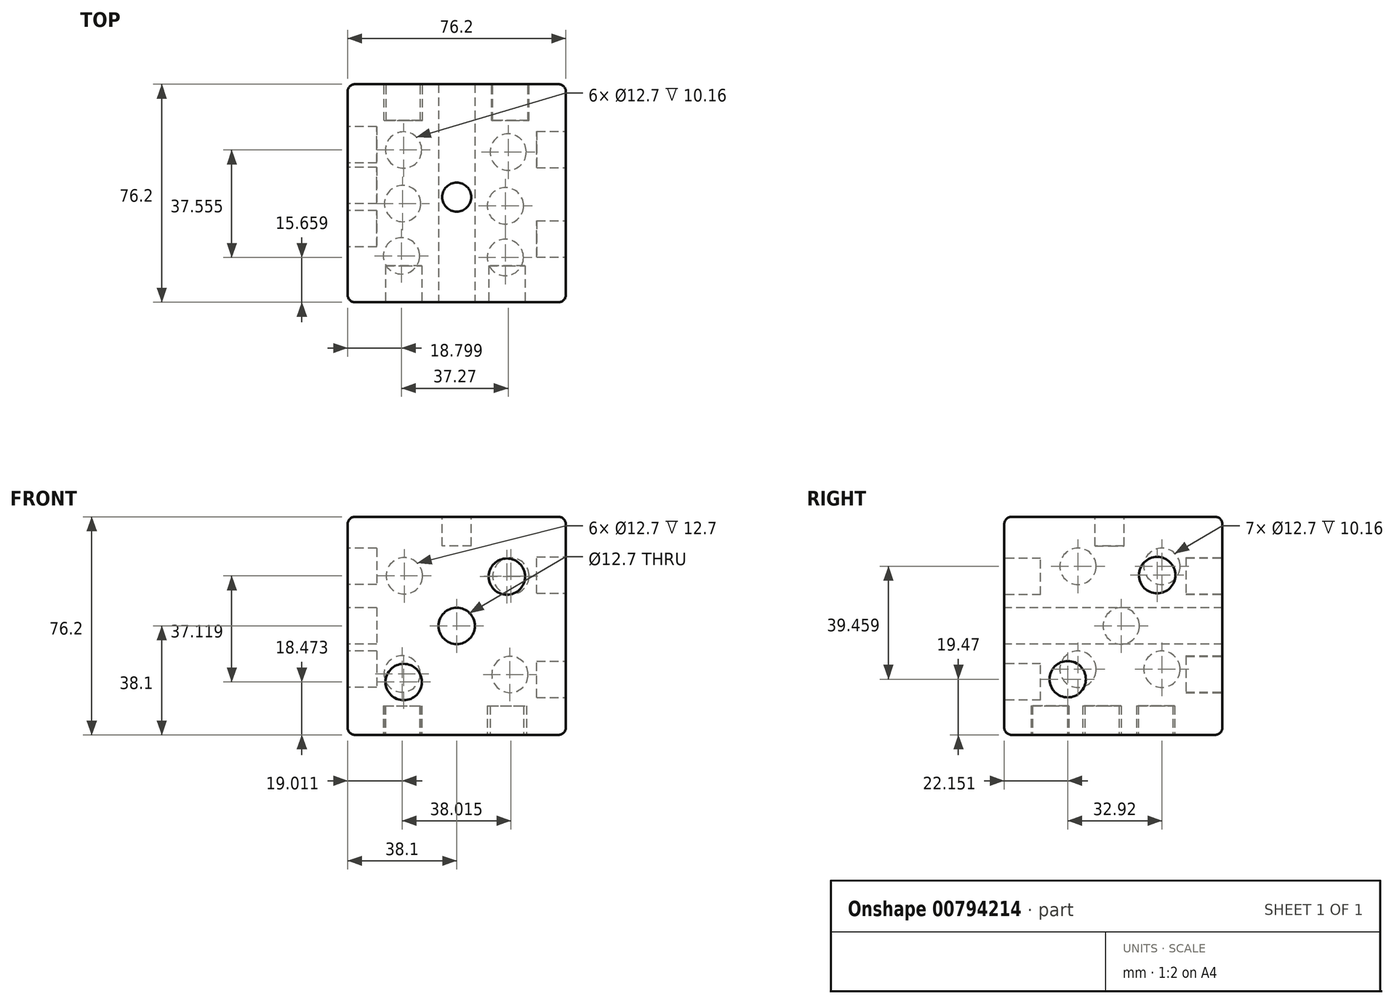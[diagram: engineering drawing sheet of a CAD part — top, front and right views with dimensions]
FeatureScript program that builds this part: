
annotation { "Feature Type Name" : "Feature", "Feature Type Description" : "" }
export const myFeature = defineFeature(function(context is Context, id is Id, definition is map)
    precondition{}
    {
        {
            var Q0;
            Q0=qCreatedBy(makeId("Front.planeOp"),FACE);
            var sketch = newSketch(context, id + "F0", { "sketchPlane" : qUnion([Q0])});
            skLineSegment(sketch, "E0.bottom", {"start": v(38.1, -38.1) * mm, "end": v(-38.1, -38.1) * mm});
            skLineSegment(sketch, "E0.top", {"start": v(38.1, 38.1) * mm, "end": v(-38.1, 38.1) * mm});
            skLineSegment(sketch, "E0.left", {"start": v(38.1, -38.1) * mm, "end": v(38.1, 38.1) * mm});
            skLineSegment(sketch, "E0.right", {"start": v(-38.1, -38.1) * mm, "end": v(-38.1, 38.1) * mm});
            skPoint(sketch, "E0.middle", {"position": v(0, 0) * mm});
            skSolve(sketch);
        }
        {
            var Q0;
            Q0=makeQuery(id+"F0.imprint","IMPRINT",FACE,{"disambiguationData":[TD([[makeQuery(id+"F0.imprint","IMPRINT",EDGE,{"derivedFrom":sQuery(id+"F0.wireOp",EDGE,"E0.bottom")}),-1.0]])]});
            extrude(context, id + "F1", {"entities" : qUnion([Q0]), "depth" : 76.2 * mm, "offsetDistance" : 25.4 * mm});
        }
        {
            var Q0;
            Q0=makeQuery(id+"F1.opExtrude","CAP_EDGE",EDGE,{"disambiguationData":[OSD([sQuery(id+"F0.wireOp",EDGE,"E0.top")])],"isStart":true});
            var Q1;
            Q1=makeQuery(id+"F1.opExtrude","SWEPT_EDGE",EDGE,{"disambiguationData":[OSD([sQuery(id+"F0.wireOp",EDGE,"E0.top"),sQuery(id+"F0.wireOp",EDGE,"E0.right")])]});
            var Q2;
            Q2=makeQuery(id+"F1.opExtrude","CAP_EDGE",EDGE,{"disambiguationData":[OSD([sQuery(id+"F0.wireOp",EDGE,"E0.right")])],"isStart":true});
            var Q3;
            Q3=makeQuery(id+"F1.opExtrude","CAP_EDGE",EDGE,{"disambiguationData":[OSD([sQuery(id+"F0.wireOp",EDGE,"E0.right")])],"isStart":false});
            var Q4;
            Q4=makeQuery(id+"F1.opExtrude","CAP_EDGE",EDGE,{"disambiguationData":[OSD([sQuery(id+"F0.wireOp",EDGE,"E0.top")])],"isStart":false});
            var Q5;
            Q5=makeQuery(id+"F1.opExtrude","CAP_EDGE",EDGE,{"disambiguationData":[OSD([sQuery(id+"F0.wireOp",EDGE,"E0.bottom")])],"isStart":false});
            var Q6;
            Q6=makeQuery(id+"F1.opExtrude","CAP_EDGE",EDGE,{"disambiguationData":[OSD([sQuery(id+"F0.wireOp",EDGE,"E0.left")])],"isStart":false});
            var Q7;
            Q7=makeQuery(id+"F1.opExtrude","SWEPT_FACE",FACE,{"disambiguationData":[OSD([sQuery(id+"F0.wireOp",EDGE,"E0.right")])]});
            var Q8;
            Q8=makeQuery(id+"F1.opExtrude","SWEPT_EDGE",EDGE,{"disambiguationData":[OSD([sQuery(id+"F0.wireOp",EDGE,"E0.bottom"),sQuery(id+"F0.wireOp",EDGE,"E0.left")])]});
            var Q9;
            Q9=makeQuery(id+"F1.opExtrude","CAP_EDGE",EDGE,{"disambiguationData":[OSD([sQuery(id+"F0.wireOp",EDGE,"E0.bottom")])],"isStart":true});
            var Q10;
            Q10=makeQuery(id+"F1.opExtrude","CAP_EDGE",EDGE,{"disambiguationData":[OSD([sQuery(id+"F0.wireOp",EDGE,"E0.left")])],"isStart":true});
            var Q11;
            Q11=makeQuery(id+"F1.opExtrude","SWEPT_EDGE",EDGE,{"disambiguationData":[OSD([sQuery(id+"F0.wireOp",EDGE,"E0.top"),sQuery(id+"F0.wireOp",EDGE,"E0.left")])]});
            fillet(context, id + "F2", {"entities" : qUnion([Q0, Q1, Q2, Q3, Q4, Q5, Q6, Q7, Q8, Q9, Q10, Q11]), "radius" : 2.54 * mm, "tangentPropagation" : true, "allowEdgeOverflow" : false});
        }
        {
            var Q0;
            Q0=makeQuery(id+"F1.opExtrude","SWEPT_FACE",FACE,{"disambiguationData":[OSD([sQuery(id+"F0.wireOp",EDGE,"E0.top")])]});
            var sketch = newSketch(context, id + "F3", { "sketchPlane" : qUnion([Q0])});
            skCircle(sketch, "E1", {"center": v(0, -39.43) * mm, "radius": 5.08 * mm});
            skSolve(sketch);
        }
        {
            var Q0;
            Q0 = qSketchRegion(id + "F3", true);
            extrude(context, id + "F4", {"entities" : qUnion([Q0]), "operationType" : NewBodyOperationType.REMOVE, "oppositeDirection" : true, "depth" : 10.16 * mm, "offsetDistance" : 25.4 * mm});
        }
        {
            var Q0;
            Q0=makeQuery(id+"F1.opExtrude","CAP_FACE",FACE,{"disambiguationData":[OSD([sQuery(id+"F0.wireOp",EDGE,"E0.bottom"),sQuery(id+"F0.wireOp",EDGE,"E0.top"),sQuery(id+"F0.wireOp",EDGE,"E0.left"),sQuery(id+"F0.wireOp",EDGE,"E0.right")])],"isStart":false});
            var sketch = newSketch(context, id + "F5", { "sketchPlane" : qUnion([Q0])});
            skCircle(sketch, "E2", {"center": v(-18.53, -19.63) * mm, "radius": 6.35 * mm});
            skCircle(sketch, "E3", {"center": v(17.52, 17.22) * mm, "radius": 6.35 * mm});
            skCircle(sketch, "E4", {"center": v(0, 0) * mm, "radius": 6.35 * mm});
            skSolve(sketch);
        }
        {
            var Q0;
            Q0 = qSketchRegion(id + "F5", true);
            extrude(context, id + "F6", {"entities" : qUnion([Q0]), "operationType" : NewBodyOperationType.REMOVE, "oppositeDirection" : true, "depth" : 12.7 * mm, "offsetDistance" : 25.4 * mm});
        }
        {
            var Q0;
            Q0=makeQuery(id+"F6.boolean.opBoolean","COPY",FACE,{"derivedFrom":makeQuery(id+"F6.opExtrude","CAP_FACE",FACE,{"disambiguationData":[OSD([sQuery(id+"F5.wireOp",EDGE,"E4")])],"isStart":false})});
            extrude(context, id + "F7", {"entities" : qUnion([Q0]), "operationType" : NewBodyOperationType.REMOVE, "oppositeDirection" : true, "depth" : 2540 * mm, "offsetDistance" : 25.4 * mm});
        }
        {
            var Q0;
            Q0=makeQuery(id+"F1.opExtrude","CAP_FACE",FACE,{"disambiguationData":[OSD([sQuery(id+"F0.wireOp",EDGE,"E0.bottom"),sQuery(id+"F0.wireOp",EDGE,"E0.top"),sQuery(id+"F0.wireOp",EDGE,"E0.left"),sQuery(id+"F0.wireOp",EDGE,"E0.right")])],"isStart":true});
            var sketch = newSketch(context, id + "F8", { "sketchPlane" : qUnion([Q0])});
            skCircle(sketch, "E5", {"center": v(-18.93, 17.42) * mm, "radius": 6.35 * mm});
            skCircle(sketch, "E6", {"center": v(18.3, 17.5) * mm, "radius": 6.35 * mm});
            skCircle(sketch, "E7", {"center": v(-18.6, -16.97) * mm, "radius": 6.35 * mm});
            skCircle(sketch, "E8", {"center": v(19.09, -16.8) * mm, "radius": 6.35 * mm});
            skSolve(sketch);
        }
        {
            var Q0;
            Q0 = qSketchRegion(id + "F8", true);
            extrude(context, id + "F9", {"entities" : qUnion([Q0]), "operationType" : NewBodyOperationType.REMOVE, "oppositeDirection" : true, "depth" : 12.7 * mm, "offsetDistance" : 25.4 * mm});
        }
        {
            var Q0;
            Q0=makeQuery(id+"F1.opExtrude","SWEPT_FACE",FACE,{"disambiguationData":[OSD([sQuery(id+"F0.wireOp",EDGE,"E0.bottom")])]});
            var sketch = newSketch(context, id + "F10", { "sketchPlane" : qUnion([Q0])});
            skCircle(sketch, "E9", {"center": v(-19.3, 60) * mm, "radius": 6.35 * mm});
            skCircle(sketch, "E10", {"center": v(-18.9, 41.7) * mm, "radius": 6.35 * mm});
            skCircle(sketch, "E11", {"center": v(16.96, 60.54) * mm, "radius": 6.35 * mm});
            skCircle(sketch, "E12", {"center": v(17.02, 42.47) * mm, "radius": 6.35 * mm});
            skCircle(sketch, "E13", {"center": v(17.97, 23.7) * mm, "radius": 6.35 * mm});
            skCircle(sketch, "E14", {"center": v(-18.58, 22.99) * mm, "radius": 6.35 * mm});
            skSolve(sketch);
        }
        {
            var Q0;
            Q0 = qSketchRegion(id + "F10", true);
            extrude(context, id + "F11", {"entities" : qUnion([Q0]), "operationType" : NewBodyOperationType.REMOVE, "oppositeDirection" : true, "depth" : 10.16 * mm, "offsetDistance" : 25.4 * mm});
        }
        {
            var Q0;
            Q0=makeQuery(id+"F1.opExtrude","SWEPT_FACE",FACE,{"disambiguationData":[OSD([sQuery(id+"F0.wireOp",EDGE,"E0.left")])]});
            var sketch = newSketch(context, id + "F12", { "sketchPlane" : qUnion([Q0])});
            skCircle(sketch, "E15", {"center": v(-22.8, 17.74) * mm, "radius": 6.35 * mm});
            skCircle(sketch, "E16", {"center": v(-54.05, -18.63) * mm, "radius": 6.35 * mm});
            skSolve(sketch);
        }
        {
            var Q0;
            Q0 = qSketchRegion(id + "F12", true);
            extrude(context, id + "F13", {"entities" : qUnion([Q0]), "operationType" : NewBodyOperationType.REMOVE, "oppositeDirection" : true, "depth" : 10.16 * mm, "offsetDistance" : 25.4 * mm});
        }
        {
            var Q0;
            Q0=makeQuery(id+"F1.opExtrude","SWEPT_FACE",FACE,{"disambiguationData":[OSD([sQuery(id+"F0.wireOp",EDGE,"E0.right")])]});
            var sketch = newSketch(context, id + "F14", { "sketchPlane" : qUnion([Q0])});
            skCircle(sketch, "E17", {"center": v(21.13, 20.83) * mm, "radius": 6.35 * mm});
            skCircle(sketch, "E18", {"center": v(50.46, 20.83) * mm, "radius": 6.35 * mm});
            skCircle(sketch, "E19", {"center": v(21.13, -15.15) * mm, "radius": 6.35 * mm});
            skCircle(sketch, "E20", {"center": v(50.46, -15.15) * mm, "radius": 6.35 * mm});
            skCircle(sketch, "E21", {"center": v(35.35, 0) * mm, "radius": 6.35 * mm});
            skSolve(sketch);
        }
        {
            var Q0;
            Q0 = qSketchRegion(id + "F14", true);
            extrude(context, id + "F15", {"entities" : qUnion([Q0]), "operationType" : NewBodyOperationType.REMOVE, "oppositeDirection" : true, "depth" : 10.16 * mm, "offsetDistance" : 25.4 * mm});
        }
    });
